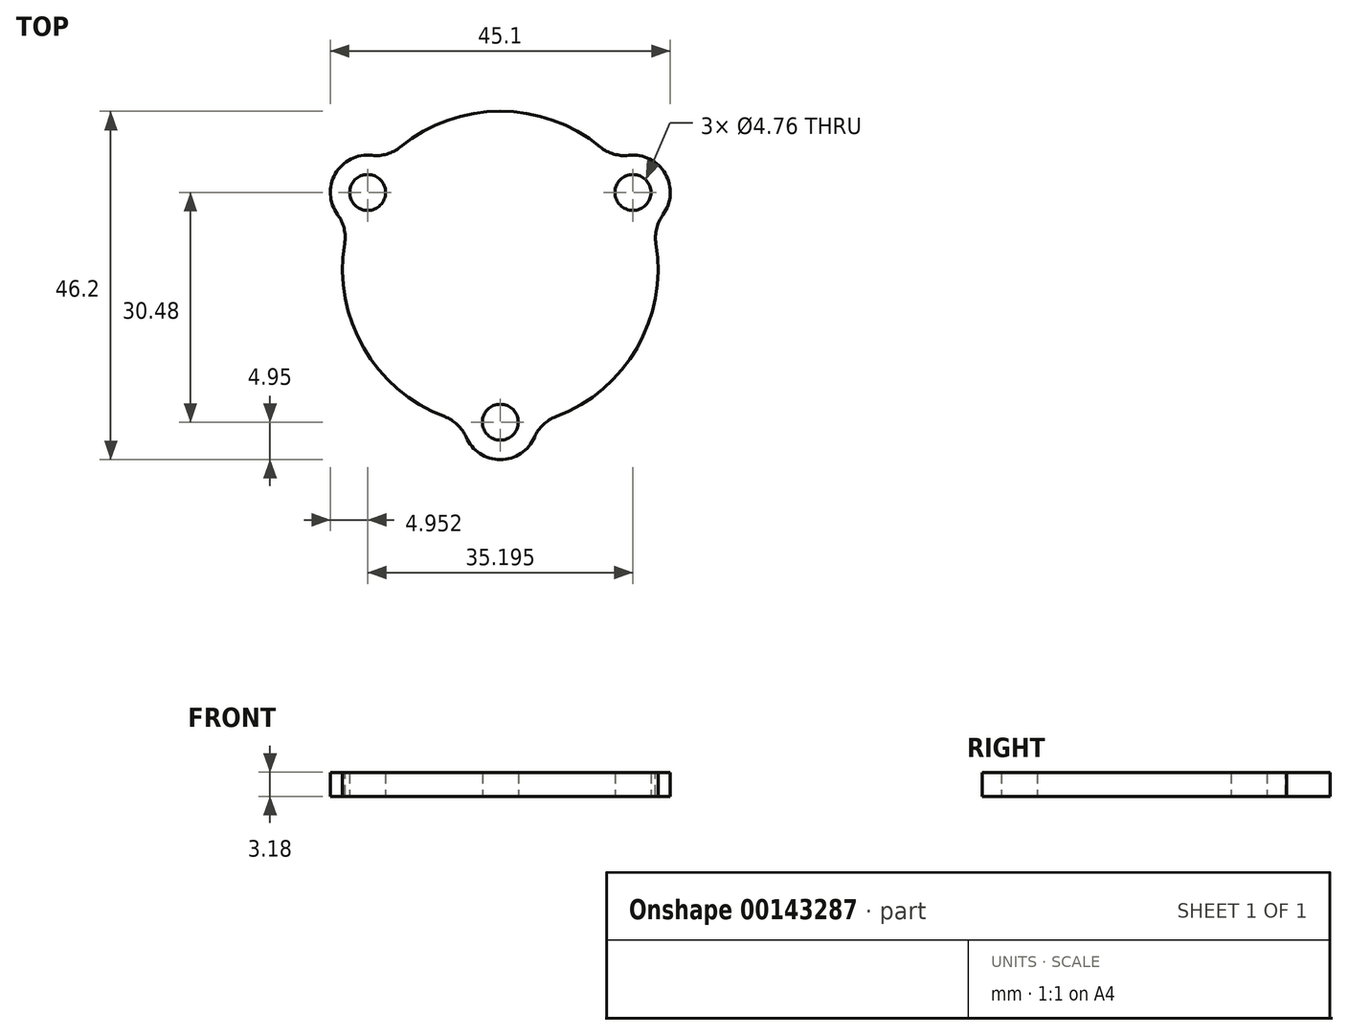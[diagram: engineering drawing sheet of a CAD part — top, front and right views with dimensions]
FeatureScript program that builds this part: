
annotation { "Feature Type Name" : "Feature", "Feature Type Description" : "" }
export const myFeature = defineFeature(function(context is Context, id is Id, definition is map)
    precondition{}
    {
        {
            var Q0;
            Q0=qCreatedBy(makeId("Front.planeOp"),FACE);
            var sketch = newSketch(context, id + "F0", { "sketchPlane" : qUnion([Q0])});
            skCircle(sketch, "E0", {"center": v(0, -12.7) * mm, "radius": 12.7 * mm});
            skLineSegment(sketch, "E1", {"start": v(-12.7, 3.17) * mm, "end": v(12.7, 3.17) * mm});
            skLineSegment(sketch, "E2", {"start": v(12.7, 3.17) * mm, "end": v(-6.95, 3.17) * mm});
            skLineSegment(sketch, "E3", {"start": v(-12.7, 3.17) * mm, "end": v(-12.7, -22.23) * mm});
            skLineSegment(sketch, "E4", {"start": v(-12.7, -22.23) * mm, "end": v(-12.7, 3.17) * mm});
            skLineSegment(sketch, "E5", {"start": v(12.7, 3.17) * mm, "end": v(12.7, -22.22) * mm});
            skLineSegment(sketch, "E6", {"start": v(12.7, -22.22) * mm, "end": v(12.7, 3.17) * mm});
            skCircle(sketch, "E7", {"center": v(-9.53, 0) * mm, "radius": 3.18 * mm});
            skPoint(sketch, "E8.visualSharp", {"position": v(-12.7, 3.17) * mm});
            skCircle(sketch, "E9", {"center": v(9.52, 0) * mm, "radius": 3.18 * mm});
            skLineSegment(sketch, "E10", {"start": v(-9.53, 0) * mm, "end": v(9.52, 0) * mm});
            skPoint(sketch, "E11", {"position": v(0, 0) * mm});
            skLineSegment(sketch, "E12", {"start": v(-12.7, -22.23) * mm, "end": v(-9.52, -22.23) * mm});
            skLineSegment(sketch, "E13", {"start": v(-9.52, -22.23) * mm, "end": v(-12.7, -22.23) * mm});
            skLineSegment(sketch, "E14", {"start": v(12.7, -22.22) * mm, "end": v(9.52, -22.22) * mm});
            skLineSegment(sketch, "E15", {"start": v(9.52, -22.22) * mm, "end": v(12.7, -22.22) * mm});
            skArc(sketch, "E16", {"start": v(-12.7, -17.2) * mm, "mid": v(-11.4, -19.89) * mm, "end": v(-9.52, -22.23) * mm});
            skArc(sketch, "E17", {"start": v(9.52, -22.22) * mm, "mid": v(11.4, -19.89) * mm, "end": v(12.7, -17.2) * mm});
            skSolve(sketch);
        }
        {
            var Q0;
            Q0=qCreatedBy(makeId("Front.planeOp"),FACE);
            var sketch = newSketch(context, id + "F1", { "sketchPlane" : qUnion([Q0])});
            skLineSegment(sketch, "E18", {"start": v(12.3, -17.56) * mm, "end": v(16.38, -17.56) * mm});
            skLineSegment(sketch, "E19", {"start": v(16.38, -17.56) * mm, "end": v(16.38, 3.17) * mm});
            skLineSegment(sketch, "E20", {"start": v(0, 3.17) * mm, "end": v(13.2, 3.18) * mm});
            skLineSegment(sketch, "E21", {"start": v(13.2, 3.17) * mm, "end": v(13.2, -11.92) * mm});
            skLineSegment(sketch, "E22", {"start": v(13.2, -11.92) * mm, "end": v(13.2, 3.17) * mm});
            skLineSegment(sketch, "E23", {"start": v(16.38, 3.17) * mm, "end": v(13.2, 3.17) * mm});
            skLineSegment(sketch, "E24", {"start": v(13.2, 3.17) * mm, "end": v(13.2, 3.17) * mm});
            skLineSegment(sketch, "E25", {"start": v(16.38, 3.17) * mm, "end": v(25.27, 3.17) * mm});
            skLineSegment(sketch, "E26", {"start": v(25.27, 3.17) * mm, "end": v(25.27, 0) * mm});
            skLineSegment(sketch, "E27", {"start": v(25.27, 0) * mm, "end": v(16.38, 0) * mm});
            skArc(sketch, "E28", {"start": v(12.3, -17.56) * mm, "mid": v(13.07, -14.79) * mm, "end": v(13.2, -11.92) * mm});
            skLineSegment(sketch, "E29", {"start": v(0, 3.17) * mm, "end": v(0, -22.11) * mm});
            skLineSegment(sketch, "E30", {"start": v(0, -22.11) * mm, "end": v(0, 3.17) * mm});
            skSolve(sketch);
        }
        {
            var Q0;
            {var subQ3=sQuery(id+"F1.wireOp",EDGE,"E18");Q0=makeQuery(id+"F1.imprint","IMPRINT",FACE,{"disambiguationData":[TD([[makeQuery(id+"F1.imprint","IMPRINT",EDGE,{"derivedFrom":subQ3}),1.0]])]});}
            var Q1;
            {var subQ0=sQuery(id+"F1.wireOp",EDGE,"E25");Q1=makeQuery(id+"F1.imprint","IMPRINT",FACE,{"disambiguationData":[TD([[makeQuery(id+"F1.imprint","IMPRINT",EDGE,{"derivedFrom":subQ0}),-1.0]])]});}
            var Q2;
            Q2=sQuery(id+"F1.wireOp",EDGE,"E30");
            revolve(context, id + "F2", {"surfaceOperationType" : NewSurfaceOperationType.NEW, "entities" : qUnion([Q0, Q1]), "axis" : qUnion([Q2]), "revolveType" : RevolveType.FULL});
        }
        {
            var Q0;
            Q0=makeQuery(id+"F2.opRevolve","SWEPT_FACE",FACE,{"disambiguationData":[OSD([sQuery(id+"F1.wireOp",EDGE,"E27")])]});
            var sketch = newSketch(context, id + "F3", { "sketchPlane" : qUnion([Q0])});
            skLineSegment(sketch, "E31", {"start": v(0, 0) * mm, "end": v(0, 20.32) * mm});
            skCircle(sketch, "E32", {"center": v(0, 20.32) * mm, "radius": 2.38 * mm});
            skCircle(sketch, "E33.1.0", {"center": v(-17.6, -10.16) * mm, "radius": 2.38 * mm});
            skCircle(sketch, "E33.2.0", {"center": v(17.6, -10.16) * mm, "radius": 2.38 * mm});
            skPoint(sketch, "E33.center", {"position": v(0, 0) * mm});
            skSolve(sketch);
        }
        {
            var Q0;
            Q0=qSketchRegion(id+"F3",true);
            extrude(context, id + "F4", {"entities" : qUnion([Q0]), "operationType" : NewBodyOperationType.REMOVE, "endBound" : BoundingType.THROUGH_ALL, "oppositeDirection" : true, "depth" : 25.4 * mm, "offsetDistance" : 25.4 * mm});
        }
        {
            var Q0;
            Q0=makeQuery(id+"F2.opRevolve","SWEPT_EDGE",EDGE,{"disambiguationData":[OSD([sQuery(id+"F1.wireOp",EDGE,"E18"),sQuery(id+"F1.wireOp",EDGE,"E19")])]});
            fillet(context, id + "F5", {"entities" : qUnion([Q0]), "radius" : 5.08 * mm, "tangentPropagation" : true, "allowEdgeOverflow" : false});
        }
        {
            var Q0;
            Q0=makeQuery(id+"F2.opRevolve","SWEPT_FACE",FACE,{"disambiguationData":[OSD([sQuery(id+"F1.wireOp",EDGE,"E27")])]});
            var sketch = newSketch(context, id + "F6", { "sketchPlane" : qUnion([Q0])});
            skCircle(sketch, "E34", {"center": v(0, 20.32) * mm, "radius": 4.95 * mm});
            skCircle(sketch, "E35", {"center": v(17.6, -10.16) * mm, "radius": 4.95 * mm});
            skCircle(sketch, "E36", {"center": v(-17.6, -10.16) * mm, "radius": 4.95 * mm});
            skArc(sketch, "E37", {"start": v(-4.95, 20.34) * mm, "mid": v(-18.13, 10.47) * mm, "end": v(-20.1, -5.88) * mm});
            skArc(sketch, "E38.1.0", {"start": v(-15.14, -14.46) * mm, "mid": v(0, -20.93) * mm, "end": v(15.14, -14.46) * mm});
            skArc(sketch, "E38.2.0", {"start": v(20.1, -5.88) * mm, "mid": v(18.13, 10.47) * mm, "end": v(4.95, 20.34) * mm});
            skCircle(sketch, "E39", {"center": v(0, 0) * mm, "radius": 25.27 * mm});
            skSolve(sketch);
        }
        {
            var Q0;
            {var subQ0=sQuery(id+"F6.wireOp",EDGE,"E37");Q0=makeQuery(id+"F6.imprint","IMPRINT",FACE,{"disambiguationData":[TD([[makeQuery(id+"F6.imprint","IMPRINT",EDGE,{"derivedFrom":subQ0}),-1.0]])]});}
            var Q1;
            {var subQ0=sQuery(id+"F6.wireOp",EDGE,"E38.2.0");Q1=makeQuery(id+"F6.imprint","IMPRINT",FACE,{"disambiguationData":[TD([[makeQuery(id+"F6.imprint","IMPRINT",EDGE,{"derivedFrom":subQ0}),-1.0]])]});}
            var Q2;
            {var subQ0=sQuery(id+"F6.wireOp",EDGE,"E38.1.0");Q2=makeQuery(id+"F6.imprint","IMPRINT",FACE,{"disambiguationData":[TD([[makeQuery(id+"F6.imprint","IMPRINT",EDGE,{"derivedFrom":subQ0}),-1.0]])]});}
            extrude(context, id + "F7", {"entities" : qUnion([Q0, Q1, Q2]), "operationType" : NewBodyOperationType.REMOVE, "endBound" : BoundingType.THROUGH_ALL, "oppositeDirection" : true, "depth" : 25.4 * mm, "offsetDistance" : 25.4 * mm});
        }
        {
            var Q0;
            Q0=makeQuery(id+"F7.boolean.opBoolean","COPY",EDGE,{"derivedFrom":makeQuery(id+"F7.opExtrude","SWEPT_EDGE",EDGE,{"disambiguationData":[OSD([sQuery(id+"F6.wireOp",EDGE,"E36"),sQuery(id+"F6.wireOp",EDGE,"E38.1.0")])]})});
            var Q1;
            Q1=makeQuery(id+"F7.boolean.opBoolean","COPY",EDGE,{"derivedFrom":makeQuery(id+"F7.opExtrude","SWEPT_EDGE",EDGE,{"disambiguationData":[OSD([sQuery(id+"F6.wireOp",EDGE,"E35"),sQuery(id+"F6.wireOp",EDGE,"E38.1.0")])]})});
            var Q2;
            Q2=makeQuery(id+"F7.boolean.opBoolean","COPY",EDGE,{"derivedFrom":makeQuery(id+"F7.opExtrude","SWEPT_EDGE",EDGE,{"disambiguationData":[OSD([sQuery(id+"F6.wireOp",EDGE,"E35"),sQuery(id+"F6.wireOp",EDGE,"E38.2.0")])]})});
            var Q3;
            Q3=makeQuery(id+"F7.boolean.opBoolean","COPY",EDGE,{"derivedFrom":makeQuery(id+"F7.opExtrude","SWEPT_EDGE",EDGE,{"disambiguationData":[OSD([sQuery(id+"F6.wireOp",EDGE,"E34"),sQuery(id+"F6.wireOp",EDGE,"E38.2.0")])]})});
            var Q4;
            Q4=makeQuery(id+"F7.boolean.opBoolean","COPY",EDGE,{"derivedFrom":makeQuery(id+"F7.opExtrude","SWEPT_EDGE",EDGE,{"disambiguationData":[OSD([sQuery(id+"F6.wireOp",EDGE,"E34"),sQuery(id+"F6.wireOp",EDGE,"E37")])]})});
            var Q5;
            Q5=makeQuery(id+"F7.boolean.opBoolean","COPY",EDGE,{"derivedFrom":makeQuery(id+"F7.opExtrude","SWEPT_EDGE",EDGE,{"disambiguationData":[OSD([sQuery(id+"F6.wireOp",EDGE,"E36"),sQuery(id+"F6.wireOp",EDGE,"E37")])]})});
            fillet(context, id + "F8", {"entities" : qUnion([Q0, Q1, Q2, Q3, Q4, Q5]), "radius" : 5.08 * mm, "tangentPropagation" : true, "allowEdgeOverflow" : false});
        }
        {
            var Q0;
            Q0=qCreatedBy(makeId("Top.planeOp"),FACE);
            var sketch = newSketch(context, id + "F9", { "sketchPlane" : qUnion([Q0])});
            skCircle(sketch, "E40", {"center": v(0, 0) * mm, "radius": 27.63 * mm});
            skSolve(sketch);
        }
        {
            var Q0;
            Q0 = qSketchRegion(id + "F9", true);
            extrude(context, id + "F10", {"entities" : qUnion([Q0]), "operationType" : NewBodyOperationType.REMOVE, "endBound" : BoundingType.THROUGH_ALL, "oppositeDirection" : true, "depth" : 25.4 * mm, "offsetDistance" : 25.4 * mm});
        }
        {
            var Q0;
            Q0=makeQuery(id+"F10.boolean.opBoolean","MERGE",FACE,{"derivedFrom":[makeQuery(id+"F2.opRevolve","SWEPT_FACE",FACE,{"disambiguationData":[OSD([sQuery(id+"F1.wireOp",EDGE,"E27")])]}),makeQuery(id+"F10.opExtrude","CAP_FACE",FACE,{"disambiguationData":[OSD([sQuery(id+"F9.wireOp",EDGE,"E40")])],"isStart":true})]});
            var sketch = newSketch(context, id + "F11", { "sketchPlane" : qUnion([Q0])});
            skCircle(sketch, "E41", {"center": v(0, 0) * mm, "radius": 14.54 * mm});
            skSolve(sketch);
        }
        {
            var Q0;
            Q0 = qSketchRegion(id + "F11", true);
            extrude(context, id + "F12", {"entities" : qUnion([Q0]), "operationType" : NewBodyOperationType.ADD, "oppositeDirection" : true, "depth" : 3.17 * mm, "offsetDistance" : 25.4 * mm});
        }
    });
